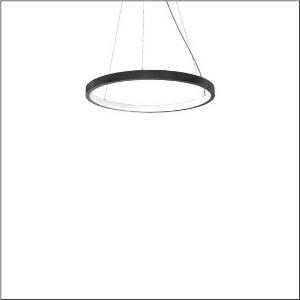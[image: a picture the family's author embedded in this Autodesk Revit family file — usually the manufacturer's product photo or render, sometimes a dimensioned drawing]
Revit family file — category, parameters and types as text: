
# Revit family: silica_r__21_ring-i_5pjbi2d3104a_3dac
name_source: partatom
category: Lighting Fixtures
units: mm (PartAtom-declared; Revit-internal decimal feet)

## family parameters
Cut with Voids When Loaded = No
Host = Face
Light Source = No
Part Type = Normal
Room Calculation Point = No
Round Connector Dimension = Use Diameter
Shared = No

## types (1)
- Silica® 21 Ring-I (1 x LED, 5040 lm, 80 W, 4000K)
    Apparent Load = 80 VA
    CIE Flux Codes = 22 48 76 50 101
    Color Rendering = 80
    Color Temperature = 4000K
    Default Elevation = 1800 mm
    Description = Silica® 21 Ring-I, suspended luminaire, of PMMA, frosted, light emission: inner ring side luminous distribution, primary light characteristic: symmetric, installation type: suspended mounting, LED, rated luminous flux: 5.040lm, luminous efficacy: 63lm/W, light colour: 840, colour temperature: 4000K, control gear: DALI 2, with terminal, 5-pole, mains connection: 230V, AC/DC, 0/50..60Hz, rated input power: 80W, housing, of extruded aluminium section, jet black (RAL 9005), diameter: 805mm, ceiling canopy, jet black (RAL 9005), protection rating (lamp compartment): IP40, insulation class (complete): insulation class I (protective earthing), certification: CE, impact resistance: IK02, permissible operating ambient temperature: 0..+35°C, packaging unit: 1 piece
    Height = 48 mm  [stored 0.15748 ft]
    Lamp = 1 x LED
    Lamp Light Flux = 5040 lm
    Lamp Power = 80 W
    Lamp count = 1
    Length = 805 mm
    Luminous efficacy = 63 lm/W
    Manufacturer = Siteco
    ModVariant = No
    Model = 5PJBI2D3104A
    Mounting Place = Ceiling
    Mounting Type = Pendant
    Number of Poles = 1
    OnlyDefault = Yes
    Power Factor = 1
    Product Name = Silica® 21 Ring-I
    Product group = suspended luminaire
    ProductGroupID = 905
    Protection Class = Protection class I
    Protection Degree = IP 40
    RLX_Detail_Level = 1
    RLX_Emergency_Light_Flux = 0 lm
    RLX_Emergency_Type = 0
    RLX_Emergency_Type_DB = No
    RlxData = <blob elided: 13945 chars, md5=e14766b1>
    Socket = socket
    Standby Power = 0 W
    System Light Flux = 5040 lm
    System Power = 80 W
    Type Comments = Product without accessories
    Type Image = l_1258365.jpg
    URL = http://relux.com
    VarID = ---
    Voltage = 0 V
    Weight = 0.00 kg
    Width = 0 mm  [stored 0 ft]

note: [stored X ft] marks values corroborated as IEEE doubles in the binary element streams (Revit-internal decimal feet)

## geometry (parser evidence)
native form markers: Sweep x14
no freeform markers — native parametric forms only
